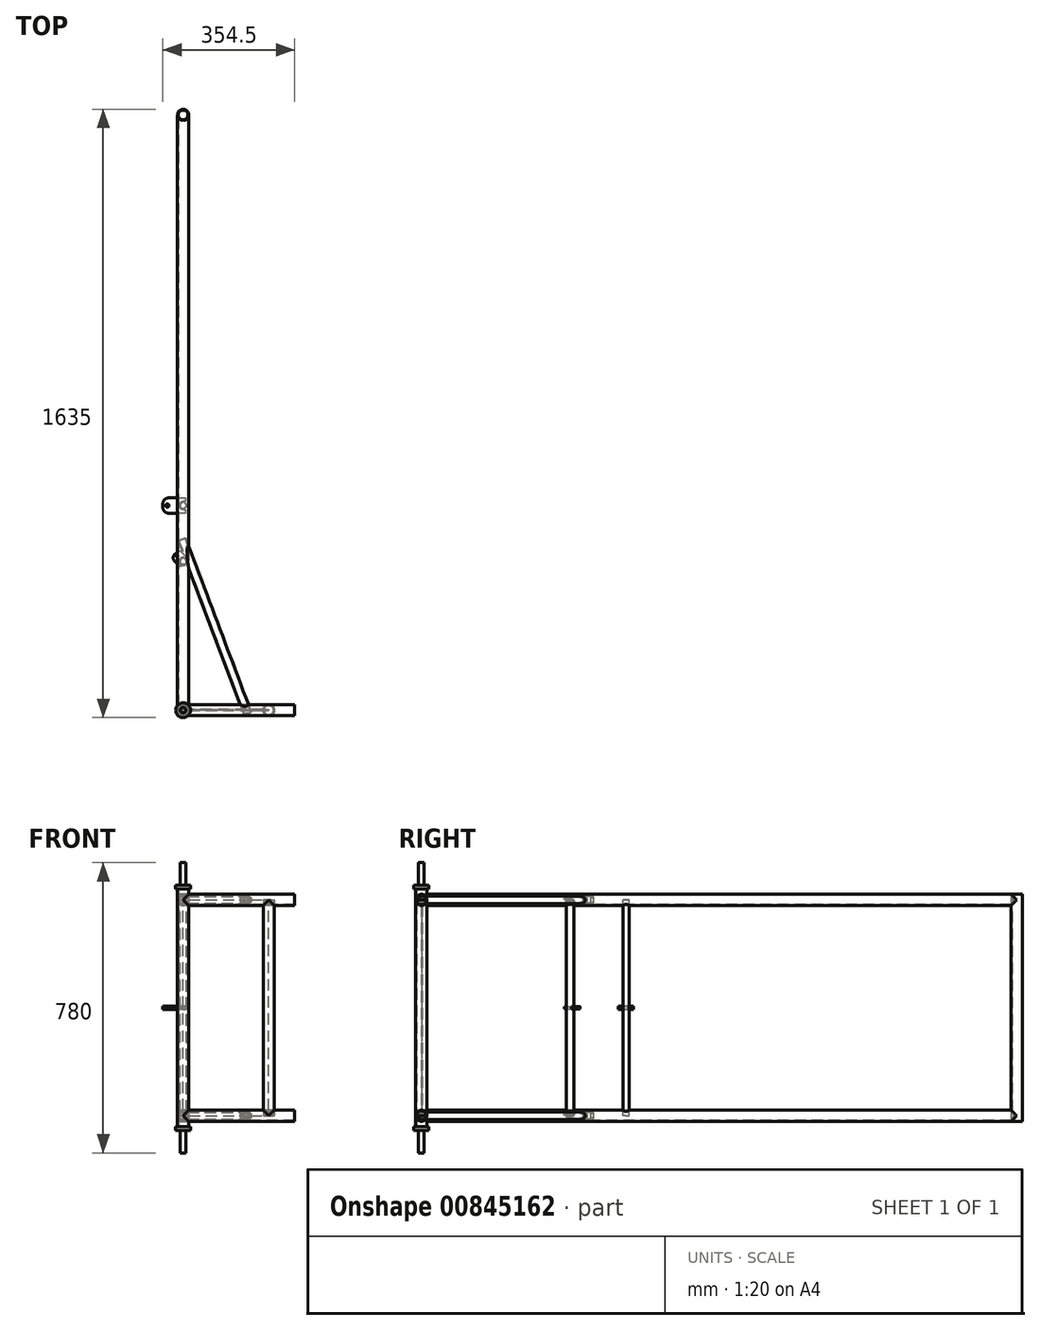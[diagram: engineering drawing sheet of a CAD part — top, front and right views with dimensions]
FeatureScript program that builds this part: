
annotation { "Feature Type Name" : "Feature", "Feature Type Description" : "" }
export const myFeature = defineFeature(function(context is Context, id is Id, definition is map)
    precondition{}
    {
        {
            var Q0;
            Q0=qCreatedBy(makeId("Top.planeOp"),FACE);
            var sketch = newSketch(context, id + "F0", { "sketchPlane" : qUnion([Q0])});
            skCircle(sketch, "E0", {"center": v(0, 0) * mm, "radius": 15 * mm});
            skCircle(sketch, "E1", {"center": v(0, 0) * mm, "radius": 13 * mm});
            skSolve(sketch);
        }
        {
            var Q0;
            Q0 = qSketchRegion(id + "F0", true);
            extrude(context, id + "F1", {"entities" : qUnion([Q0]), "depth" : 640 * mm, "offsetDistance" : 25 * mm});
        }
        {
            var Q0;
            Q0=makeQuery(id+"F1.opExtrude","CAP_FACE",FACE,{"disambiguationData":[OSD([sQuery(id+"F0.wireOp",EDGE,"E0"),sQuery(id+"F0.wireOp",EDGE,"E1")])],"isStart":false});
            var sketch = newSketch(context, id + "F2", { "sketchPlane" : qUnion([Q0])});
            skCircle(sketch, "E2", {"center": v(0, 0) * mm, "radius": 20 * mm});
            skSolve(sketch);
        }
        {
            var Q0;
            Q0 = qSketchRegion(id + "F2", true);
            extrude(context, id + "F3", {"entities" : qUnion([Q0]), "operationType" : NewBodyOperationType.ADD, "depth" : 10 * mm, "offsetDistance" : 25 * mm});
        }
        {
            var Q0;
            Q0=makeQuery(id+"F3.opExtrude","CAP_FACE",FACE,{"disambiguationData":[OSD([sQuery(id+"F2.wireOp",EDGE,"E2")])],"isStart":false});
            var sketch = newSketch(context, id + "F4", { "sketchPlane" : qUnion([Q0])});
            skCircle(sketch, "E3", {"center": v(0, 0) * mm, "radius": 7.5 * mm});
            skSolve(sketch);
        }
        {
            var Q0;
            Q0 = qSketchRegion(id + "F4", true);
            extrude(context, id + "F5", {"entities" : qUnion([Q0]), "operationType" : NewBodyOperationType.ADD, "depth" : 60 * mm, "offsetDistance" : 25 * mm});
        }
        {
            var Q0;
            Q0=makeQuery(id+"F1.opExtrude","CAP_FACE",FACE,{"disambiguationData":[OSD([sQuery(id+"F0.wireOp",EDGE,"E0"),sQuery(id+"F0.wireOp",EDGE,"E1")])],"isStart":true});
            var sketch = newSketch(context, id + "F6", { "sketchPlane" : qUnion([Q0])});
            skCircle(sketch, "E4", {"center": v(0, 0) * mm, "radius": 20 * mm});
            skSolve(sketch);
        }
        {
            var Q0;
            Q0 = qSketchRegion(id + "F6", true);
            extrude(context, id + "F7", {"entities" : qUnion([Q0]), "operationType" : NewBodyOperationType.ADD, "depth" : 10 * mm, "offsetDistance" : 25 * mm});
        }
        {
            var Q0;
            Q0=makeQuery(id+"F7.opExtrude","CAP_FACE",FACE,{"disambiguationData":[OSD([sQuery(id+"F6.wireOp",EDGE,"E4")])],"isStart":false});
            var sketch = newSketch(context, id + "F8", { "sketchPlane" : qUnion([Q0])});
            skCircle(sketch, "E5", {"center": v(0, 0) * mm, "radius": 7.5 * mm});
            skSolve(sketch);
        }
        {
            var Q0;
            Q0 = qSketchRegion(id + "F8", true);
            extrude(context, id + "F9", {"entities" : qUnion([Q0]), "operationType" : NewBodyOperationType.ADD, "depth" : 60 * mm, "offsetDistance" : 25 * mm});
        }
        {
            var Q0;
            Q0=qCreatedBy(makeId("Right.planeOp"),FACE);
            cPlane(context, id + "F10", {"entities" : qUnion([Q0]), "cplaneType" : CPlaneType.OFFSET, "offset" : 0 * mm, "width" : 150 * mm, "height" : 150 * mm});
        }
        {
            var Q0;
            Q0=qCreatedBy(id+"F10.planeOp",FACE);
            var sketch = newSketch(context, id + "F11", { "sketchPlane" : qUnion([Q0])});
            skCircle(sketch, "E6", {"center": v(0, 30) * mm, "radius": 15 * mm});
            skCircle(sketch, "E7", {"center": v(0, 610) * mm, "radius": 15 * mm});
            skLineSegment(sketch, "E8", {"start": v(0, 30) * mm, "end": v(0, 610) * mm, "construction": true});
            skLineSegment(sketch, "E9", {"start": v(0, 30) * mm, "end": v(0, 0) * mm, "construction": true});
            skCircle(sketch, "E10", {"center": v(0, 30) * mm, "radius": 13 * mm});
            skCircle(sketch, "E11", {"center": v(0, 610) * mm, "radius": 13 * mm});
            skSolve(sketch);
        }
        {
            var Q0;
            Q0 = qSketchRegion(id + "F11", true);
            extrude(context, id + "F12", {"entities" : qUnion([Q0]), "operationType" : NewBodyOperationType.ADD, "depth" : 300 * mm, "offsetDistance" : 25 * mm});
        }
        {
            var Q0;
            Q0=qCreatedBy(makeId("Top.planeOp"),FACE);
            cPlane(context, id + "F13", {"entities" : qUnion([Q0]), "cplaneType" : CPlaneType.OFFSET, "offset" : 30 * mm, "width" : 150 * mm, "height" : 150 * mm});
        }
        {
            var Q0;
            Q0=qCreatedBy(makeId("Front.planeOp"),FACE);
            var sketch = newSketch(context, id + "F14", { "sketchPlane" : qUnion([Q0])});
            skLineSegment(sketch, "E12", {"start": v(0, 30) * mm, "end": v(230, 30) * mm});
            skLineSegment(sketch, "E13", {"start": v(230, 30) * mm, "end": v(230, 610) * mm});
            skLineSegment(sketch, "E14", {"start": v(230, 610) * mm, "end": v(0, 610) * mm});
            skSolve(sketch);
        }
        {
            var Q0;
            Q0=qCreatedBy(id+"F13.planeOp",FACE);
            var sketch = newSketch(context, id + "F15", { "sketchPlane" : qUnion([Q0])});
            skCircle(sketch, "E15", {"center": v(230, 0) * mm, "radius": 15 * mm});
            skCircle(sketch, "E16", {"center": v(230, 0) * mm, "radius": 13 * mm});
            skSolve(sketch);
        }
        {
            var Q0;
            Q0 = qSketchRegion(id + "F15", true);
            extrude(context, id + "F16", {"entities" : qUnion([Q0]), "operationType" : NewBodyOperationType.ADD, "depth" : 580 * mm, "offsetDistance" : 25 * mm});
        }
        {
            var Q0;
            Q0=qCreatedBy(makeId("Front.planeOp"),FACE);
            var sketch = newSketch(context, id + "F17", { "sketchPlane" : qUnion([Q0])});
            skCircle(sketch, "E17", {"center": v(0, 30) * mm, "radius": 15 * mm});
            skCircle(sketch, "E18", {"center": v(0, 610) * mm, "radius": 15 * mm});
            skLineSegment(sketch, "E19", {"start": v(0, 30) * mm, "end": v(0, 610) * mm});
            skLineSegment(sketch, "E20", {"start": v(0, 30) * mm, "end": v(0, 0) * mm});
            skCircle(sketch, "E21", {"center": v(0, 30) * mm, "radius": 13 * mm});
            skCircle(sketch, "E22", {"center": v(0, 610) * mm, "radius": 13 * mm});
            skSolve(sketch);
        }
        {
            var Q0;
            Q0 = qSketchRegion(id + "F17", true);
            extrude(context, id + "F18", {"entities" : qUnion([Q0]), "operationType" : NewBodyOperationType.ADD, "oppositeDirection" : true, "depth" : 1600 * mm, "offsetDistance" : 25 * mm});
        }
        {
            var Q0;
            Q0=qCreatedBy(id+"F10.planeOp",FACE);
            cPlane(context, id + "F19", {"entities" : qUnion([Q0]), "cplaneType" : CPlaneType.OFFSET, "offset" : 0 * mm, "oppositeDirection" : true, "width" : 150 * mm, "height" : 150 * mm});
        }
        {
            var Q0;
            Q0=qCreatedBy(id+"F19.planeOp",FACE);
            var sketch = newSketch(context, id + "F20", { "sketchPlane" : qUnion([Q0])});
            skLineSegment(sketch, "E23", {"start": v(0, 30) * mm, "end": v(1600, 30) * mm});
            skLineSegment(sketch, "E24", {"start": v(1600, 30) * mm, "end": v(1600, 610) * mm});
            skLineSegment(sketch, "E25", {"start": v(1600, 610) * mm, "end": v(26.13, 610) * mm});
            skLineSegment(sketch, "E26", {"start": v(550, 610) * mm, "end": v(550, 30) * mm});
            skLineSegment(sketch, "E27", {"start": v(400, 610) * mm, "end": v(400, 30) * mm});
            skSolve(sketch);
        }
        {
            var Q0;
            Q0=sQuery(id+"F20.wireOp",EDGE,"E24");
            cPlane(context, id + "F21", {"entities" : qUnion([Q0]), "cplaneType" : CPlaneType.MID_PLANE, "offset" : 25 * mm, "width" : 150 * mm, "height" : 150 * mm});
        }
        {
            var Q0;
            Q0=qCreatedBy(id+"F21.planeOp",FACE);
            var sketch = newSketch(context, id + "F22", { "sketchPlane" : qUnion([Q0])});
            skCircle(sketch, "E28", {"center": v(0, 1600) * mm, "radius": 13 * mm});
            skCircle(sketch, "E29", {"center": v(0, 1600) * mm, "radius": 15 * mm});
            skSolve(sketch);
        }
        {
            var Q0;
            Q0 = qSketchRegion(id + "F22", true);
            extrude(context, id + "F23", {"entities" : qUnion([Q0]), "operationType" : NewBodyOperationType.ADD, "depth" : 305 * mm, "offsetDistance" : 25 * mm, "hasSecondDirection" : true, "secondDirectionOppositeDirection" : true, "secondDirectionDepth" : 305 * mm});
        }
        {
            var Q0;
            Q0=makeQuery(id+"F23.opExtrude","CAP_FACE",FACE,{"disambiguationData":[OSD([sQuery(id+"F22.wireOp",EDGE,"E28"),sQuery(id+"F22.wireOp",EDGE,"E29")])],"isStart":true});
            var sketch = newSketch(context, id + "F24", { "sketchPlane" : qUnion([Q0])});
            skCircle(sketch, "E30", {"center": v(0, -1600) * mm, "radius": 13 * mm});
            skSolve(sketch);
        }
        {
            var Q0;
            Q0 = qSketchRegion(id + "F24", true);
            extrude(context, id + "F25", {"entities" : qUnion([Q0]), "operationType" : NewBodyOperationType.REMOVE, "oppositeDirection" : true, "depth" : 700 * mm, "offsetDistance" : 25 * mm});
        }
        {
            var Q0;
            Q0=sQuery(id+"F14.wireOp",EDGE,"E12");
            var Q1;
            Q1=sQuery(id+"F20.wireOp",EDGE,"E23");
            cPlane(context, id + "F26", {"entities" : qUnion([Q0, Q1]), "cplaneType" : CPlaneType.LINE_ANGLE, "offset" : 25 * mm, "angle" : 0 * degree, "width" : 150 * mm, "height" : 150 * mm});
        }
        {
            var Q0;
            Q0=qCreatedBy(id+"F26.planeOp",FACE);
            var sketch = newSketch(context, id + "F27", { "sketchPlane" : qUnion([Q0])});
            skLineSegment(sketch, "E31", {"start": v(170, 0) * mm, "end": v(0, 450) * mm});
            skLineSegment(sketch, "E32", {"start": v(170, 0) * mm, "end": v(0, 0) * mm});
            skLineSegment(sketch, "E33", {"start": v(170, 0) * mm, "end": v(230, 0) * mm});
            skSolve(sketch);
        }
        {
            var Q0;
            Q0=sQuery(id+"F27.wireOp",EDGE,"E31");
            cPlane(context, id + "F28", {"entities" : qUnion([Q0]), "cplaneType" : CPlaneType.MID_PLANE, "offset" : 25 * mm, "width" : 150 * mm, "height" : 150 * mm});
        }
        {
            var Q0;
            Q0=qCreatedBy(id+"F28.planeOp",FACE);
            var sketch = newSketch(context, id + "F29", { "sketchPlane" : qUnion([Q0])});
            skCircle(sketch, "E34", {"center": v(-159.03, 30) * mm, "radius": 8.5 * mm});
            skCircle(sketch, "E35", {"center": v(-159.03, 30) * mm, "radius": 10.5 * mm});
            skLineSegment(sketch, "E36", {"start": v(-159.03, 30) * mm, "end": v(-159.03, 610) * mm, "construction": true});
            skCircle(sketch, "E37", {"center": v(-159.03, 610) * mm, "radius": 10.5 * mm});
            skCircle(sketch, "E38", {"center": v(-159.03, 610) * mm, "radius": 8.5 * mm});
            skSolve(sketch);
        }
        {
            var Q0;
            Q0 = qSketchRegion(id + "F29", true);
            extrude(context, id + "F30", {"entities" : qUnion([Q0]), "operationType" : NewBodyOperationType.ADD, "depth" : 250 * mm, "offsetDistance" : 25 * mm, "hasSecondDirection" : true, "secondDirectionOppositeDirection" : true, "secondDirectionDepth" : 250 * mm});
        }
        {
            var Q0;
            Q0=sQuery(id+"F20.wireOp",EDGE,"E26");
            cPlane(context, id + "F31", {"entities" : qUnion([Q0]), "cplaneType" : CPlaneType.MID_PLANE, "offset" : 25 * mm, "width" : 150 * mm, "height" : 150 * mm});
        }
        {
            var Q0;
            Q0=qCreatedBy(id+"F31.planeOp",FACE);
            var sketch = newSketch(context, id + "F32", { "sketchPlane" : qUnion([Q0])});
            skCircle(sketch, "E39", {"center": v(0, -550) * mm, "radius": 10.5 * mm});
            skCircle(sketch, "E40", {"center": v(0, -550) * mm, "radius": 8.5 * mm});
            skCircle(sketch, "E41", {"center": v(0, -400) * mm, "radius": 10.5 * mm});
            skCircle(sketch, "E42", {"center": v(0, -400) * mm, "radius": 8.5 * mm});
            skLineSegment(sketch, "E43", {"start": v(0, -550) * mm, "end": v(0, -543.78) * mm, "construction": true});
            skLineSegment(sketch, "E44", {"start": v(0, -550) * mm, "end": v(-10.5, -550) * mm, "construction": true});
            skLineSegment(sketch, "E45", {"start": v(-10.5, -550) * mm, "end": v(-10.5, -550) * mm});
            skLineSegment(sketch, "E46", {"start": v(0, -539.5) * mm, "end": v(5.5, -539.5) * mm});
            skLineSegment(sketch, "E47", {"start": v(5.5, -539.5) * mm, "end": v(5.5, -529.5) * mm});
            skLineSegment(sketch, "E48", {"start": v(5.5, -529.5) * mm, "end": v(-39.5, -529.5) * mm});
            skLineSegment(sketch, "E49", {"start": v(-39.5, -570.5) * mm, "end": v(5.5, -570.5) * mm});
            skLineSegment(sketch, "E50", {"start": v(5.5, -570.5) * mm, "end": v(5.5, -560.5) * mm});
            skLineSegment(sketch, "E51", {"start": v(5.5, -560.5) * mm, "end": v(0, -560.5) * mm});
            skLineSegment(sketch, "E52", {"start": v(-54.5, -555.5) * mm, "end": v(-54.5, -544.5) * mm});
            skLineSegment(sketch, "E53", {"start": v(-10.5, -550) * mm, "end": v(-54.5, -550) * mm, "construction": true});
            skCircle(sketch, "E54", {"center": v(-42.5, -550) * mm, "radius": 4.5 * mm});
            skLineSegment(sketch, "E55", {"start": v(0, -400) * mm, "end": v(0, -434.8) * mm, "construction": true});
            skLineSegment(sketch, "E56", {"start": v(0, -400) * mm, "end": v(-7.68, -407.16) * mm, "construction": true});
            skLineSegment(sketch, "E57", {"start": v(-7.68, -407.16) * mm, "end": v(-7.68, -407.16) * mm});
            skLineSegment(sketch, "E58", {"start": v(-5.13, -383.6) * mm, "end": v(-24.18, -402.64) * mm});
            skLineSegment(sketch, "E59", {"start": v(-24.18, -416.78) * mm, "end": v(-17.06, -423.9) * mm});
            skLineSegment(sketch, "E60", {"start": v(-3.27, -424.24) * mm, "end": v(-3.17, -424.15) * mm});
            skLineSegment(sketch, "E61", {"start": v(-7.68, -407.16) * mm, "end": v(-20.74, -420.22) * mm, "construction": true});
            skLineSegment(sketch, "E62", {"start": v(7.16, -407.68) * mm, "end": v(11.18, -403.93) * mm});
            skLineSegment(sketch, "E63", {"start": v(11.18, -403.93) * mm, "end": v(14.6, -407.58) * mm});
            skLineSegment(sketch, "E64", {"start": v(14.6, -407.58) * mm, "end": v(-3.27, -424.24) * mm});
            skLineSegment(sketch, "E65", {"start": v(-7.16, -392.32) * mm, "end": v(-3.14, -388.57) * mm});
            skLineSegment(sketch, "E66", {"start": v(-3.14, -388.57) * mm, "end": v(-6.55, -384.91) * mm});
            skLineSegment(sketch, "E67", {"start": v(-5.13, -383.6) * mm, "end": v(-6.55, -384.91) * mm});
            skCircle(sketch, "E68", {"center": v(-15.08, -414.56) * mm, "radius": 3.25 * mm});
            skPoint(sketch, "E69.visualSharp", {"position": v(-10.23, -430.73) * mm});
            skArc(sketch, "E69.filletArc", {"start": v(-17.06, -423.9) * mm, "mid": v(-10.16, -426.83) * mm, "end": v(-3.17, -424.15) * mm});
            skPoint(sketch, "E70.visualSharp", {"position": v(-31.25, -409.7) * mm});
            skArc(sketch, "E70.filletArc", {"start": v(-24.18, -402.64) * mm, "mid": v(-27.1, -409.7) * mm, "end": v(-24.18, -416.78) * mm});
            skPoint(sketch, "E71.visualSharp", {"position": v(-54.5, -529.5) * mm});
            skArc(sketch, "E71.filletArc", {"start": v(-39.5, -529.5) * mm, "mid": v(-50.1, -533.9) * mm, "end": v(-54.5, -544.5) * mm});
            skPoint(sketch, "E72.visualSharp", {"position": v(-54.5, -570.5) * mm});
            skArc(sketch, "E72.filletArc", {"start": v(-54.5, -555.5) * mm, "mid": v(-50.1, -566.1) * mm, "end": v(-39.5, -570.5) * mm});
            skPoint(sketch, "E73.visualSharp", {"position": v(-0.52, -414.84) * mm});
            skArc(sketch, "E73.filletArc", {"start": v(-7.68, -407.16) * mm, "mid": v(-0.37, -410.5) * mm, "end": v(7.16, -407.68) * mm});
            skPoint(sketch, "E74.visualSharp", {"position": v(-14.84, -399.48) * mm});
            skArc(sketch, "E74.filletArc", {"start": v(-7.16, -392.32) * mm, "mid": v(-10.5, -399.63) * mm, "end": v(-7.68, -407.16) * mm});
            skPoint(sketch, "E75.visualSharp", {"position": v(-10.5, -560.5) * mm});
            skArc(sketch, "E75.filletArc", {"start": v(-10.5, -550) * mm, "mid": v(-7.42, -557.42) * mm, "end": v(0, -560.5) * mm});
            skPoint(sketch, "E76.visualSharp", {"position": v(-10.5, -539.5) * mm});
            skArc(sketch, "E76.filletArc", {"start": v(0, -539.5) * mm, "mid": v(-7.42, -542.58) * mm, "end": v(-10.5, -550) * mm});
            skSolve(sketch);
        }
        {
            var Q0;
            Q0=makeQuery(id+"F32.imprint","IMPRINT",FACE,{"disambiguationData":[TD([[makeQuery(id+"F32.imprint","IMPRINT",EDGE,{"derivedFrom":sQuery(id+"F32.wireOp",EDGE,"E40")}),1.0]])]});
            var Q1;
            Q1=makeQuery(id+"F32.imprint","IMPRINT",FACE,{"disambiguationData":[TD([[makeQuery(id+"F32.imprint","IMPRINT",EDGE,{"derivedFrom":sQuery(id+"F32.wireOp",EDGE,"E41")}),1.0]])]});
            extrude(context, id + "F33", {"entities" : qUnion([Q0, Q1]), "operationType" : NewBodyOperationType.ADD, "depth" : 290 * mm, "offsetDistance" : 25 * mm, "hasSecondDirection" : true, "secondDirectionOppositeDirection" : true, "secondDirectionDepth" : 290 * mm});
        }
        {
            var Q0;
            {var subQ1=sQuery(id+"F32.wireOp",EDGE,"E46");Q0=makeQuery(id+"F32.imprint","IMPRINT",FACE,{"disambiguationData":[TD([[makeQuery(id+"F32.imprint","IMPRINT",EDGE,{"derivedFrom":subQ1}),1.0]])]});}
            extrude(context, id + "F34", {"entities" : qUnion([Q0]), "operationType" : NewBodyOperationType.ADD, "depth" : 5 * mm, "offsetDistance" : 25 * mm, "hasSecondDirection" : true, "secondDirectionOppositeDirection" : true, "secondDirectionDepth" : 5 * mm});
        }
        {
            var Q0;
            Q0=makeQuery(id+"F32.imprint","IMPRINT",FACE,{"disambiguationData":[TD([[makeQuery(id+"F32.imprint","IMPRINT",EDGE,{"derivedFrom":sQuery(id+"F32.wireOp",EDGE,"E59")}),1.0]])]});
            extrude(context, id + "F35", {"entities" : qUnion([Q0]), "operationType" : NewBodyOperationType.ADD, "depth" : 3 * mm, "offsetDistance" : 25 * mm, "hasSecondDirection" : true, "secondDirectionOppositeDirection" : true, "secondDirectionDepth" : 3 * mm});
        }
        {
            var Q0;
            Q0=sQuery(id+"F27.wireOp",EDGE,"E32");
            var Q1;
            Q1=sQuery(id+"F17.wireOp",EDGE,"E19");
            cPlane(context, id + "F36", {"entities" : qUnion([Q0, Q1]), "cplaneType" : CPlaneType.LINE_ANGLE, "offset" : 25 * mm, "angle" : 0 * degree, "width" : 150 * mm, "height" : 150 * mm});
        }
        {
            var Q0;
            Q0=qCreatedBy(id+"F36.planeOp",FACE);
            var sketch = newSketch(context, id + "F37", { "sketchPlane" : qUnion([Q0])});
            skLineSegment(sketch, "E77.bottom", {"start": v(0, 30) * mm, "end": v(-230, 30) * mm});
            skLineSegment(sketch, "E77.top", {"start": v(0, 610) * mm, "end": v(-230, 610) * mm});
            skLineSegment(sketch, "E77.left", {"start": v(0, 30) * mm, "end": v(0, 610) * mm});
            skLineSegment(sketch, "E77.right", {"start": v(-230, 30) * mm, "end": v(-230, 610) * mm});
            skSolve(sketch);
        }
        {
            var Q0;
            Q0 = qSketchRegion(id + "F37", true);
            extrude(context, id + "F38", {"entities" : qUnion([Q0]), "operationType" : NewBodyOperationType.ADD, "depth" : 2.5 * mm, "offsetDistance" : 25 * mm});
        }
    });
